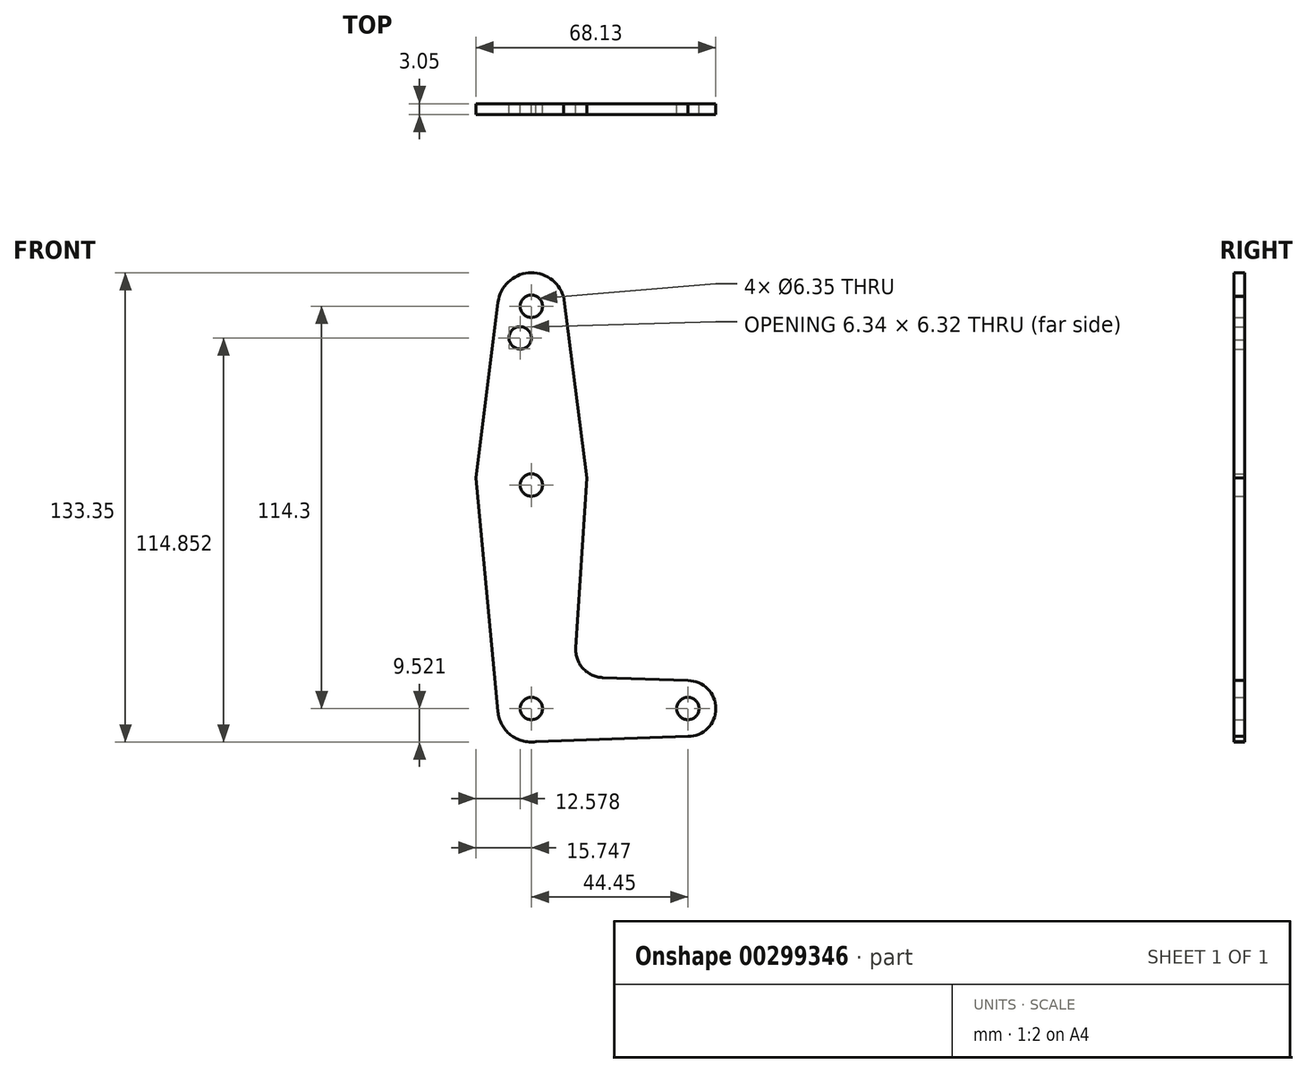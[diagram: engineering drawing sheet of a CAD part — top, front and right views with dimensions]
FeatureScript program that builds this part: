
annotation { "Feature Type Name" : "Feature", "Feature Type Description" : "" }
export const myFeature = defineFeature(function(context is Context, id is Id, definition is map)
    precondition{}
    {
        {
            var Q0;
            Q0=qCreatedBy(makeId("Front.planeOp"),FACE);
            var sketch = newSketch(context, id + "F0", { "sketchPlane" : qUnion([Q0])});
            skArc(sketch, "E0", {"start": v(-40.74, 71.7) * mm, "mid": v(-59.3, 67.66) * mm, "end": v(-40.33, 68.47) * mm});
            skArc(sketch, "E1", {"start": v(-64.94, 13.18) * mm, "mid": v(-49.4, 2.21) * mm, "end": v(-34.5, 14.03) * mm});
            skCircle(sketch, "E2", {"center": v(-49.84, -45.42) * mm, "radius": 9.53 * mm});
            skCircle(sketch, "E3", {"center": v(-5.4, -45.42) * mm, "radius": 7.94 * mm});
            skLineSegment(sketch, "E4", {"start": v(-49.84, -45.42) * mm, "end": v(-49.84, 18.08) * mm});
            skLineSegment(sketch, "E5", {"start": v(-49.84, -45.42) * mm, "end": v(-5.4, -45.42) * mm});
            skLineSegment(sketch, "E6", {"start": v(-59.3, 70.07) * mm, "end": v(-65.6, 20.07) * mm});
            skLineSegment(sketch, "E7", {"start": v(-65.6, 20.07) * mm, "end": v(-59.33, -46.31) * mm});
            skLineSegment(sketch, "E8", {"start": v(-48.6, -54.86) * mm, "end": v(-5.4, -53.36) * mm});
            skLineSegment(sketch, "E9", {"start": v(-5.4, -37.48) * mm, "end": v(-29.59, -36.61) * mm});
            skLineSegment(sketch, "E10", {"start": v(-37.24, -28.15) * mm, "end": v(-34.1, 20.1) * mm});
            skLineSegment(sketch, "E11", {"start": v(-34.1, 20.1) * mm, "end": v(-40.74, 71.7) * mm});
            skCircle(sketch, "E12", {"center": v(-49.84, 68.88) * mm, "radius": 3.18 * mm});
            skCircle(sketch, "E13", {"center": v(-49.84, 18.08) * mm, "radius": 3.18 * mm});
            skCircle(sketch, "E14", {"center": v(-49.84, -45.42) * mm, "radius": 3.18 * mm});
            skCircle(sketch, "E15", {"center": v(-5.4, -45.42) * mm, "radius": 3.18 * mm});
            skCircle(sketch, "E16", {"center": v(-53.02, 59.9) * mm, "radius": 3.18 * mm});
            skArc(sketch, "E17.filletArc", {"start": v(-37.24, -28.15) * mm, "mid": v(-35.2, -34) * mm, "end": v(-29.59, -36.61) * mm});
            skArc(sketch, "E18.trimOffspring", {"start": v(-34.1, 20.1) * mm, "mid": v(-49.87, 33.96) * mm, "end": v(-65.6, 20.07) * mm});
            skLineSegment(sketch, "E19", {"start": v(-49.84, 18.08) * mm, "end": v(-49.84, 68.88) * mm});
            skSolve(sketch);
        }
        {
            var Q0;
            Q0 = qSketchRegion(id + "F0", true);
            extrude(context, id + "F1", {"entities" : qUnion([Q0]), "depth" : 3.05 * mm});
        }
        {
            var Q0;
            {var subQ0=sQuery(id+"F0.wireOp",EDGE,"E4");var subQ1=sQuery(id+"F0.wireOp",EDGE,"E2");var subQ2=makeQuery(id+"F0.imprint","INTERSECT",VERTEX,{"derivedFrom":[subQ1,subQ0]});Q0=makeQuery(id+"F0.imprint","IMPRINT",FACE,{"disambiguationData":[TD([[makeQuery(id+"F0.imprint","IMPRINT",EDGE,{"disambiguationData":[TD([[subQ2,1.0]])],"derivedFrom":subQ1}),1.0]])]});}
            extrude(context, id + "F2", {"entities" : qUnion([Q0]), "operationType" : NewBodyOperationType.ADD, "depth" : 3.05 * mm});
        }
    });
